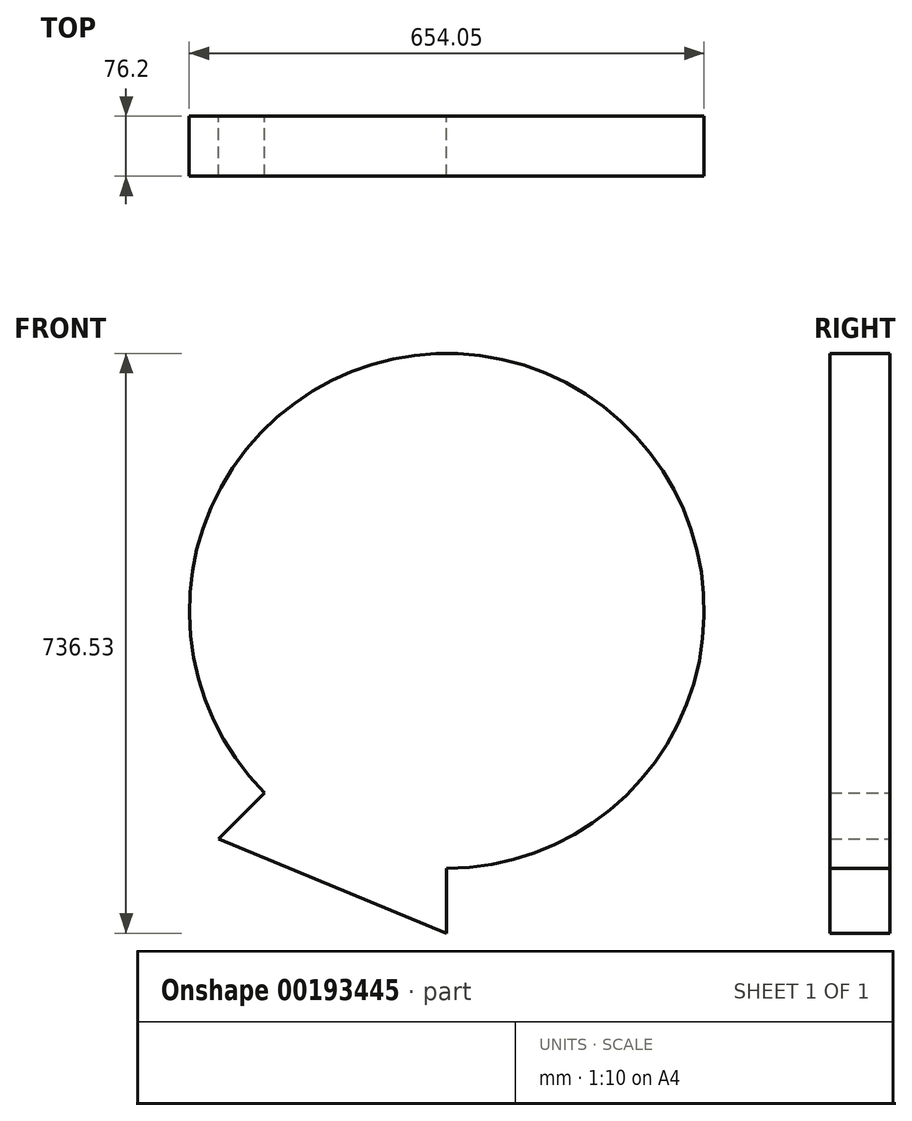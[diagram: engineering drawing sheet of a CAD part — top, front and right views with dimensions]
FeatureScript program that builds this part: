
annotation { "Feature Type Name" : "Feature", "Feature Type Description" : "" }
export const myFeature = defineFeature(function(context is Context, id is Id, definition is map)
    precondition{}
    {
        {
            var Q0;
            Q0=qCreatedBy(makeId("Front.planeOp"),FACE);
            var sketch = newSketch(context, id + "F0", { "sketchPlane" : qUnion([Q0])});
            skPoint(sketch, "E0", {"position": v(0, 0) * mm});
            skCircle(sketch, "E1", {"center": v(0, 0) * mm, "radius": 327.03 * mm});
            skPoint(sketch, "E2", {"position": v(-231.24, -231.24) * mm});
            skPoint(sketch, "E3", {"position": v(231.24, 231.24) * mm});
            skPoint(sketch, "E4", {"position": v(-231.24, 231.24) * mm});
            skPoint(sketch, "E5", {"position": v(0, 327.03) * mm});
            skPoint(sketch, "E6", {"position": v(327.03, 0) * mm});
            skPoint(sketch, "E7", {"position": v(231.24, -231.24) * mm});
            skPoint(sketch, "E8", {"position": v(0, -327.03) * mm});
            skPoint(sketch, "E9", {"position": v(-327.03, 0) * mm});
            skLineSegment(sketch, "E10", {"start": v(-327.03, 0) * mm, "end": v(-231.24, 231.24) * mm});
            skLineSegment(sketch, "E11", {"start": v(-231.24, 231.24) * mm, "end": v(0, 327.03) * mm});
            skLineSegment(sketch, "E12", {"start": v(0, 327.03) * mm, "end": v(231.24, 231.24) * mm});
            skLineSegment(sketch, "E13", {"start": v(231.24, 231.24) * mm, "end": v(327.03, 0) * mm});
            skLineSegment(sketch, "E14", {"start": v(327.03, 0) * mm, "end": v(231.24, -231.24) * mm});
            skLineSegment(sketch, "E15", {"start": v(231.24, -231.24) * mm, "end": v(0, -327.03) * mm});
            skLineSegment(sketch, "E16", {"start": v(0, -327.03) * mm, "end": v(-231.24, -231.24) * mm});
            skLineSegment(sketch, "E17", {"start": v(-231.24, -231.24) * mm, "end": v(-327.03, 0) * mm});
            skPoint(sketch, "E18", {"position": v(-260.4, 301.64) * mm});
            skPoint(sketch, "E19", {"position": v(-29.16, 397.42) * mm});
            skPoint(sketch, "E20", {"position": v(29.16, 397.42) * mm});
            skPoint(sketch, "E21", {"position": v(260.4, 301.64) * mm});
            skPoint(sketch, "E22", {"position": v(301.64, 260.4) * mm});
            skPoint(sketch, "E23", {"position": v(397.42, 29.16) * mm});
            skPoint(sketch, "E24", {"position": v(397.42, -29.16) * mm});
            skPoint(sketch, "E25", {"position": v(301.64, -260.4) * mm});
            skPoint(sketch, "E26", {"position": v(260.4, -301.64) * mm});
            skPoint(sketch, "E27", {"position": v(29.16, -397.42) * mm});
            skPoint(sketch, "E28", {"position": v(-29.16, -397.42) * mm});
            skPoint(sketch, "E29", {"position": v(-260.4, -301.64) * mm});
            skPoint(sketch, "E30", {"position": v(-301.64, -260.4) * mm});
            skPoint(sketch, "E31", {"position": v(-397.42, -29.16) * mm});
            skPoint(sketch, "E32", {"position": v(-397.42, 29.16) * mm});
            skPoint(sketch, "E33", {"position": v(-301.64, 260.4) * mm});
            skLineSegment(sketch, "E34", {"start": v(231.24, 231.24) * mm, "end": v(-231.24, -231.24) * mm});
            skLineSegment(sketch, "E35", {"start": v(0, -327.03) * mm, "end": v(0, 327.03) * mm});
            skLineSegment(sketch, "E36", {"start": v(-231.24, 231.24) * mm, "end": v(231.24, -231.24) * mm});
            skLineSegment(sketch, "E37", {"start": v(327.03, 0) * mm, "end": v(-327.03, 0) * mm});
            skLineSegment(sketch, "E38", {"start": v(0, 327.03) * mm, "end": v(0, 496.1) * mm});
            skLineSegment(sketch, "E39", {"start": v(231.24, 231.24) * mm, "end": v(527.8, 527.8) * mm});
            skLineSegment(sketch, "E40", {"start": v(327.03, 0) * mm, "end": v(621.99, 0) * mm});
            skLineSegment(sketch, "E41", {"start": v(231.24, -231.24) * mm, "end": v(382.48, -382.48) * mm});
            skLineSegment(sketch, "E42", {"start": v(0, -327.03) * mm, "end": v(0, -455.39) * mm});
            skLineSegment(sketch, "E43", {"start": v(-231.24, -231.24) * mm, "end": v(-422.26, -422.26) * mm});
            skLineSegment(sketch, "E44", {"start": v(-327.03, 0) * mm, "end": v(-507.02, 0) * mm});
            skLineSegment(sketch, "E45", {"start": v(-231.24, 231.24) * mm, "end": v(-430.88, 430.88) * mm});
            skPoint(sketch, "E46", {"position": v(0, -409.5) * mm});
            skPoint(sketch, "E47", {"position": v(-289.56, -289.56) * mm});
            skLineSegment(sketch, "E48", {"start": v(0, -409.5) * mm, "end": v(-289.56, -289.56) * mm});
            skSolve(sketch);
        }
        {
            var Q0;
            Q0 = qSketchRegion(id + "F0", true);
            extrude(context, id + "F1", {"entities" : qUnion([Q0]), "depth" : 76.2 * mm});
        }
    });
